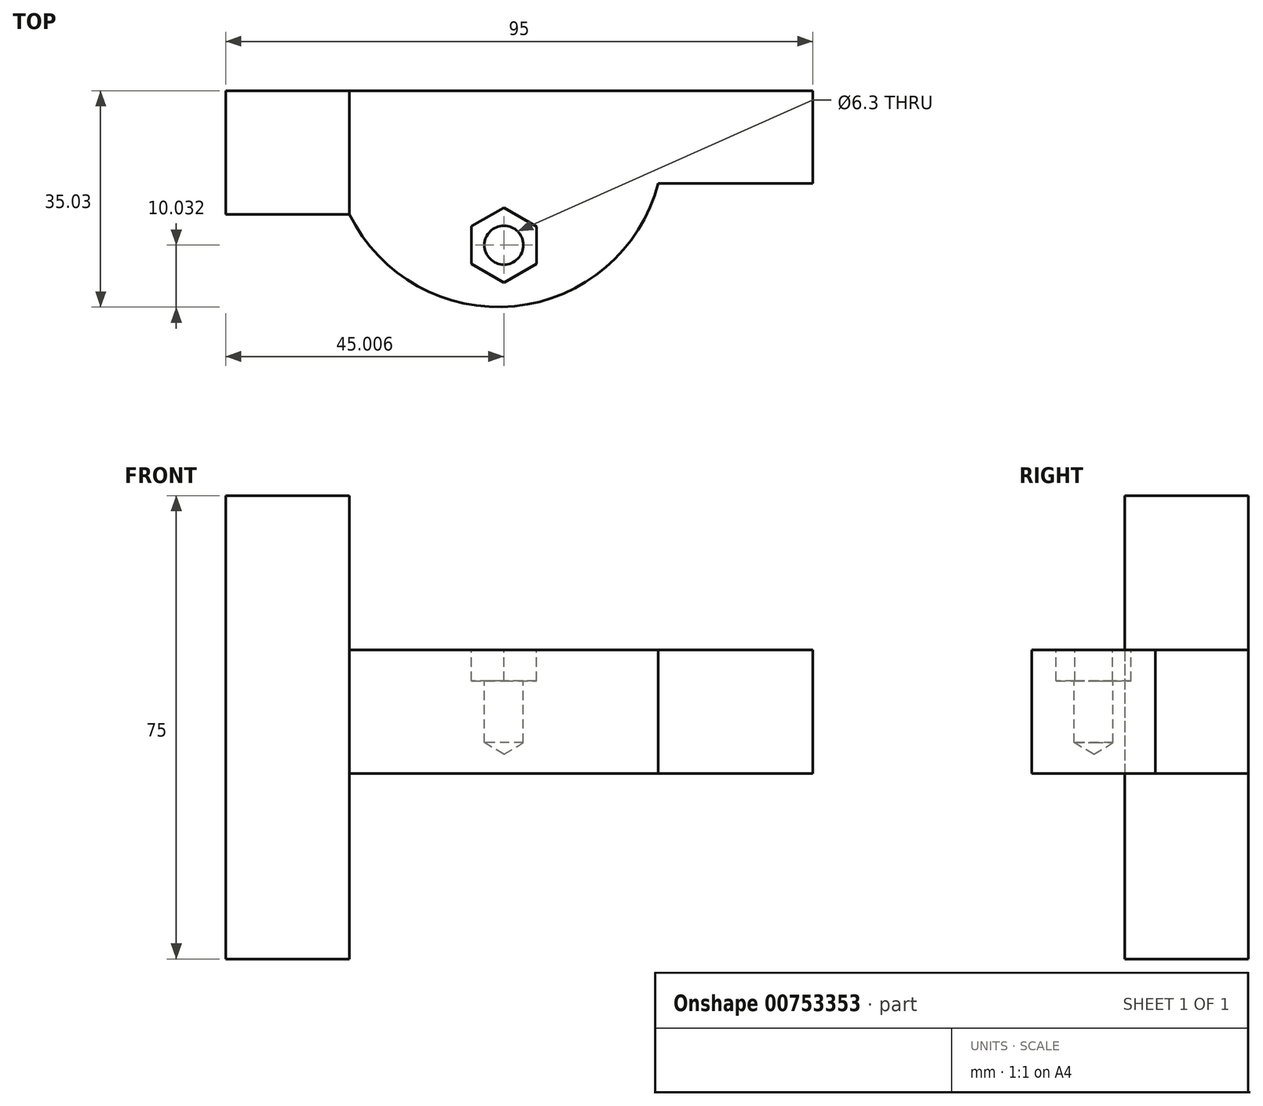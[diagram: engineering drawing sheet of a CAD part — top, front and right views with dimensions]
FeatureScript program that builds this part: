
annotation { "Feature Type Name" : "Feature", "Feature Type Description" : "" }
export const myFeature = defineFeature(function(context is Context, id is Id, definition is map)
    precondition{}
    {
        {
            var Q0;
            Q0=qCreatedBy(makeId("Front.planeOp"),FACE);
            var sketch = newSketch(context, id + "F0", { "sketchPlane" : qUnion([Q0])});
            skLineSegment(sketch, "E0", {"start": v(-45, 35) * mm, "end": v(-45, -40) * mm});
            skLineSegment(sketch, "E1", {"start": v(-45, -40) * mm, "end": v(-25, -40) * mm});
            skLineSegment(sketch, "E2", {"start": v(-25, -40) * mm, "end": v(-25, -10) * mm});
            skLineSegment(sketch, "E3", {"start": v(50, -10) * mm, "end": v(50, 10) * mm});
            skLineSegment(sketch, "E4", {"start": v(50, 10) * mm, "end": v(-25, 10) * mm});
            skLineSegment(sketch, "E5", {"start": v(-25, 10) * mm, "end": v(-25, 35) * mm});
            skLineSegment(sketch, "E6", {"start": v(-25, 35) * mm, "end": v(-45, 35) * mm});
            skLineSegment(sketch, "E7", {"start": v(50, -10) * mm, "end": v(-25, -10) * mm});
            skLineSegment(sketch, "E8", {"start": v(-25, 10) * mm, "end": v(-25, -10) * mm});
            skSolve(sketch);
        }
        {
            var Q0;
            Q0=makeQuery(id+"F0.imprint","IMPRINT",FACE,{"disambiguationData":[TD([[makeQuery(id+"F0.imprint","IMPRINT",EDGE,{"derivedFrom":sQuery(id+"F0.wireOp",EDGE,"E0")}),1.0]])]});
            extrude(context, id + "F1", {"entities" : qUnion([Q0]), "depth" : 20 * mm, "offsetDistance" : 25 * mm});
        }
        {
            var Q0;
            Q0=makeQuery(id+"F0.imprint","IMPRINT",FACE,{"disambiguationData":[TD([[makeQuery(id+"F0.imprint","IMPRINT",EDGE,{"derivedFrom":sQuery(id+"F0.wireOp",EDGE,"E3")}),1.0]])]});
            extrude(context, id + "F2", {"entities" : qUnion([Q0]), "operationType" : NewBodyOperationType.ADD, "depth" : 15 * mm, "offsetDistance" : 25 * mm});
        }
        {
            var Q0;
            Q0=qCreatedBy(makeId("Top.planeOp"),FACE);
            var sketch = newSketch(context, id + "F3", { "sketchPlane" : qUnion([Q0])});
            skLineSegment(sketch, "E9", {"start": v(0, -25) * mm, "end": v(0, 0) * mm});
            skPoint(sketch, "E10", {"position": v(-25, -20) * mm});
            skPoint(sketch, "E11", {"position": v(25, -15) * mm});
            skArc(sketch, "E12", {"start": v(-25, -20) * mm, "mid": v(1.74, -34.9) * mm, "end": v(25, -15) * mm});
            skLineSegment(sketch, "E13", {"start": v(-25, -20) * mm, "end": v(-25, -15) * mm});
            skLineSegment(sketch, "E14", {"start": v(-25, -15) * mm, "end": v(25, -15) * mm});
            skSolve(sketch);
        }
        {
            var Q0;
            {var subQ0=sQuery(id+"F3.wireOp",EDGE,"E12");Q0=makeQuery(id+"F3.imprint","IMPRINT",FACE,{"disambiguationData":[TD([[makeQuery(id+"F3.imprint","IMPRINT",EDGE,{"derivedFrom":subQ0}),1.0]])]});}
            extrude(context, id + "F4", {"entities" : qUnion([Q0]), "operationType" : NewBodyOperationType.ADD, "endBound" : BoundingType.SYMMETRIC, "depth" : 20 * mm, "offsetDistance" : 25 * mm});
        }
        {
            var Q0;
            Q0=makeQuery(id+"F4.boolean.opBoolean","MERGE",FACE,{"derivedFrom":[makeQuery(id+"F2.opExtrude","SWEPT_FACE",FACE,{"disambiguationData":[OSD([sQuery(id+"F0.wireOp",EDGE,"E4")])]}),makeQuery(id+"F4.opExtrude","CAP_FACE",FACE,{"disambiguationData":[OSD([sQuery(id+"F3.wireOp",EDGE,"E12"),sQuery(id+"F3.wireOp",EDGE,"E13"),sQuery(id+"F3.wireOp",EDGE,"E14")])],"isStart":false})]});
            var sketch = newSketch(context, id + "F5", { "sketchPlane" : qUnion([Q0])});
            skCircle(sketch, "E15.cCircle", {"center": v(0, -25) * mm, "radius": 5.25 * mm, "construction": true});
            skLineSegment(sketch, "E15.0", {"start": v(0, -18.94) * mm, "end": v(5.26, -21.97) * mm});
            skLineSegment(sketch, "E15.1", {"start": v(5.26, -21.97) * mm, "end": v(5.25, -28.03) * mm});
            skLineSegment(sketch, "E15.2", {"start": v(5.25, -28.03) * mm, "end": v(0, -31.06) * mm});
            skLineSegment(sketch, "E15.3", {"start": v(0, -31.06) * mm, "end": v(-5.25, -28.03) * mm});
            skLineSegment(sketch, "E15.4", {"start": v(-5.25, -28.03) * mm, "end": v(-5.24, -21.96) * mm});
            skLineSegment(sketch, "E15.5", {"start": v(-5.24, -21.96) * mm, "end": v(0, -18.94) * mm});
            skPoint(sketch, "E15.0.midPoint", {"position": v(2.63, -20.45) * mm});
            skSolve(sketch);
        }
        {
            var Q0;
            Q0=makeQuery(id+"F5.imprint","IMPRINT",FACE,{"disambiguationData":[TD([[makeQuery(id+"F5.imprint","IMPRINT",EDGE,{"derivedFrom":sQuery(id+"F5.wireOp",EDGE,"E15.0")}),-1.0]])]});
            extrude(context, id + "F6", {"entities" : qUnion([Q0]), "operationType" : NewBodyOperationType.REMOVE, "oppositeDirection" : true, "depth" : 5 * mm, "offsetDistance" : 25 * mm});
        }
        {
            var Q0;
            Q0=sQuery(id+"F5.wireOp",VERTEX,"E15.cCircle.center");
            var Q1;
            Q1=makeQuery(id+"F1.opExtrude","SWEPT_BODY",BODY,{"disambiguationData":[OSD([sQuery(id+"F0.wireOp",EDGE,"E0"),sQuery(id+"F0.wireOp",EDGE,"E1"),sQuery(id+"F0.wireOp",EDGE,"E2"),sQuery(id+"F0.wireOp",EDGE,"E5"),sQuery(id+"F0.wireOp",EDGE,"E6"),sQuery(id+"F0.wireOp",EDGE,"E8")])]});
            hole(context, id + "F7", {"style" : HoleStyle.SIMPLE, "endStyle" : HoleEndStyle.BLIND, "standardTappedOrClearance" : lookupTablePath({ "fit" : "Close", "standard" : "ISO", "size" : "M6", "type" : "Clearance" }), "standardBlindInLast" : lookupTablePath({ "fit" : "Close", "standard" : "ISO", "size" : "M6", "type" : "Clearance" }), "holeDiameter" : 6.3 * mm, "majorDiameter" : 5 * mm, "holeDepth" : 15 * mm, "isTappedThrough" : true, "tappedDepth" : 12 * mm, "tapClearance" : 3, "startFromSketch" : true, "locations" : qUnion([Q0]), "scope" : qUnion([Q1])});
        }
    });
